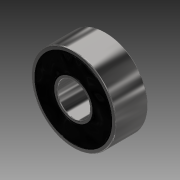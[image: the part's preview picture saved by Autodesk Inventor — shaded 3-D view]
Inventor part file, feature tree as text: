
AUTODESK INVENTOR PART (.ipt)
format: ipt  version: 2018 (Build 220112000, 112)  size: 195,584 bytes
history: native  units: in
note: dims shown in document units (in); Inventor stores cm internally (conversion verified against a paired STEP export)
features: sketch x2, extrude x1, fillet x1, revolve x1, plane x1, mirror x1
ambient origin geometry x8: Origin, YZ Plane, XZ Plane, XY Plane, X Axis, Y Axis, Z Axis, Center Point
bodies: Solid1 (feature_tree)
feature tree (7):
  extrude  "Extrusion1"  Depth=0.3937in
  fillet  "Fillet1"  Radius=0.3937in
  revolve  "Revolution1"  Angle=90.0deg
  plane  "Work Plane2"
  mirror  "Mirror2"
  sketch  "Sketch1"  dims[d0=0.3937in d1=1.0236in d2=0.3937in d3=0.0in]
  sketch  "Sketch2"  dims[d4=0.0118in d5=90.0deg d6=0.0197in d7=-0.1969in]
